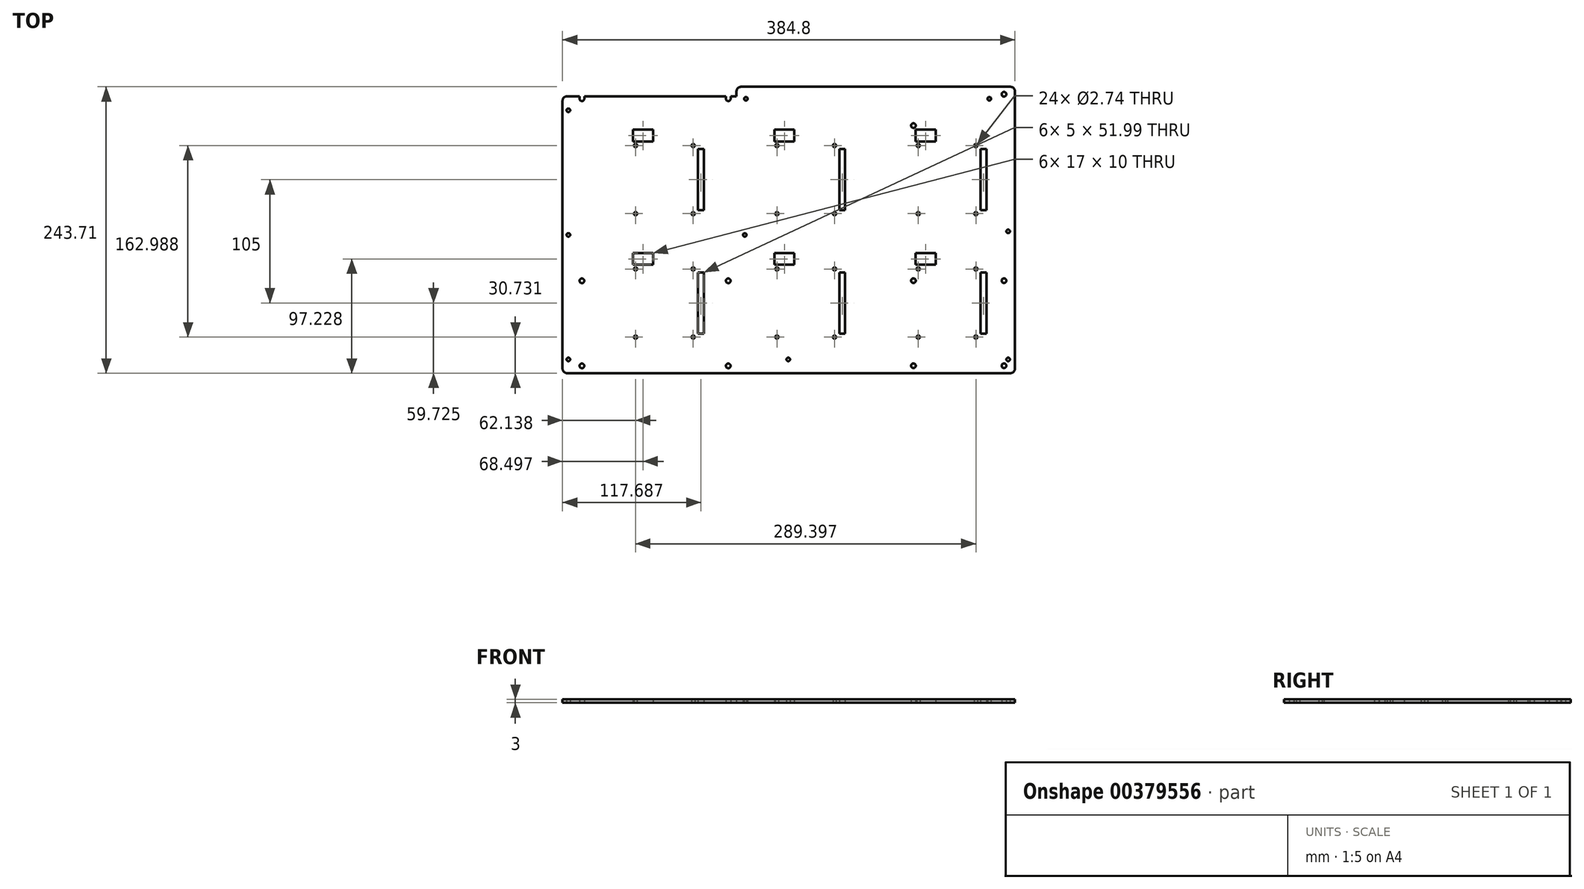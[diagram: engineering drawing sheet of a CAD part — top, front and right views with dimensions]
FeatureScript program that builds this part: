
annotation { "Feature Type Name" : "Feature", "Feature Type Description" : "" }
export const myFeature = defineFeature(function(context is Context, id is Id, definition is map)
    precondition{}
    {
        {
            var Q0;
            Q0=qCreatedBy(makeId("Top.planeOp"),FACE);
            var sketch = newSketch(context, id + "F0", { "sketchPlane" : qUnion([Q0])});
            skLineSegment(sketch, "E0.bottom", {"start": v(-157.61, -121.94) * mm, "end": v(139.26, -121.94) * mm});
            skLineSegment(sketch, "E0.left", {"start": v(-161.57, -117.98) * mm, "end": v(-161.57, 109.8) * mm});
            skArc(sketch, "E1", {"start": v(-147.04, 111.6) * mm, "mid": v(-145.06, 109.63) * mm, "end": v(-143.08, 111.6) * mm});
            skCircle(sketch, "E2", {"center": v(-145.06, -115.72) * mm, "radius": 1.98 * mm});
            skCircle(sketch, "E3", {"center": v(-145.06, -43.33) * mm, "radius": 1.98 * mm});
            skCircle(sketch, "E4", {"center": v(-20.6, -115.72) * mm, "radius": 1.98 * mm});
            skArc(sketch, "E5", {"start": v(-22.58, 111.6) * mm, "mid": v(-20.6, 109.63) * mm, "end": v(-18.62, 111.6) * mm});
            skCircle(sketch, "E6", {"center": v(136.88, 88.75) * mm, "radius": 1.98 * mm});
            skCircle(sketch, "E7", {"center": v(136.88, -115.6) * mm, "radius": 1.98 * mm});
            skCircle(sketch, "E8", {"center": v(136.88, -43.2) * mm, "radius": 1.98 * mm});
            skPoint(sketch, "E9.visualSharp", {"position": v(-161.57, -121.94) * mm});
            skArc(sketch, "E9.filletArc", {"start": v(-161.57, -117.98) * mm, "mid": v(-160.41, -120.78) * mm, "end": v(-157.61, -121.94) * mm});
            skCircle(sketch, "E10.MirrorC", {"center": v(-50.44, 13.8) * mm, "radius": 1.37 * mm});
            skCircle(sketch, "E11.MirrorC", {"center": v(-99.43, 71.78) * mm, "radius": 1.37 * mm});
            skCircle(sketch, "E12.MirrorC", {"center": v(-99.43, 13.8) * mm, "radius": 1.37 * mm});
            skCircle(sketch, "E13.MirrorC", {"center": v(-50.44, 71.78) * mm, "radius": 1.37 * mm});
            skLineSegment(sketch, "E14.bottom", {"start": v(-46.38, 68.78) * mm, "end": v(-41.38, 68.78) * mm});
            skLineSegment(sketch, "E14.top", {"start": v(-46.38, 16.8) * mm, "end": v(-41.38, 16.8) * mm});
            skLineSegment(sketch, "E14.left", {"start": v(-46.38, 68.78) * mm, "end": v(-46.38, 16.8) * mm});
            skLineSegment(sketch, "E14.right", {"start": v(-41.38, 68.78) * mm, "end": v(-41.38, 16.8) * mm});
            skCircle(sketch, "E15.MirrorC", {"center": v(-20.6, -43.33) * mm, "radius": 1.98 * mm});
            skCircle(sketch, "E16", {"center": v(-5.6, 111.6) * mm, "radius": 1.5 * mm});
            skCircle(sketch, "E17", {"center": v(-156.57, 101.77) * mm, "radius": 1.5 * mm});
            skLineSegment(sketch, "E18", {"start": v(-157.61, 113.77) * mm, "end": v(-147.04, 113.77) * mm});
            skLineSegment(sketch, "E19", {"start": v(-13.6, 117.8) * mm, "end": v(-13.6, 117.8) * mm});
            skLineSegment(sketch, "E20.trimOffspring", {"start": v(-9.64, 121.77) * mm, "end": v(143.23, 121.77) * mm});
            skPoint(sketch, "E21.visualSharp", {"position": v(-161.57, 113.77) * mm});
            skArc(sketch, "E21.filletArc", {"start": v(-157.61, 113.77) * mm, "mid": v(-160.41, 112.6) * mm, "end": v(-161.57, 109.8) * mm});
            skPoint(sketch, "E22.visualSharp", {"position": v(-13.6, 121.77) * mm});
            skArc(sketch, "E22.filletArc", {"start": v(-9.64, 121.77) * mm, "mid": v(-12.44, 120.6) * mm, "end": v(-13.6, 117.8) * mm});
            skPoint(sketch, "E23.visualSharp", {"position": v(-13.6, 113.77) * mm});
            skLineSegment(sketch, "E24", {"start": v(-147.04, 111.6) * mm, "end": v(-147.04, 113.77) * mm});
            skLineSegment(sketch, "E25", {"start": v(-143.08, 111.6) * mm, "end": v(-143.08, 113.77) * mm});
            skLineSegment(sketch, "E26.trimOffspring", {"start": v(-143.08, 113.77) * mm, "end": v(-22.58, 113.77) * mm, "construction": true});
            skLineSegment(sketch, "E27.trimOffspring", {"start": v(-143.08, 113.77) * mm, "end": v(-22.58, 113.77) * mm});
            skLineSegment(sketch, "E28", {"start": v(-22.58, 111.6) * mm, "end": v(-22.58, 113.77) * mm});
            skLineSegment(sketch, "E29", {"start": v(-18.62, 111.6) * mm, "end": v(-18.62, 113.77) * mm});
            skLineSegment(sketch, "E30.trimOffspring", {"start": v(-18.62, 113.77) * mm, "end": v(-13.6, 113.77) * mm});
            skLineSegment(sketch, "E31", {"start": v(-13.6, 113.77) * mm, "end": v(-13.6, 113.77) * mm});
            skLineSegment(sketch, "E32", {"start": v(-13.6, 113.77) * mm, "end": v(-13.6, 117.8) * mm});
            skLineSegment(sketch, "E33.bottom", {"start": v(-101.57, 85.29) * mm, "end": v(-84.57, 85.29) * mm});
            skLineSegment(sketch, "E33.top", {"start": v(-101.57, 75.29) * mm, "end": v(-84.57, 75.29) * mm});
            skLineSegment(sketch, "E33.left", {"start": v(-101.57, 85.29) * mm, "end": v(-101.57, 75.29) * mm});
            skLineSegment(sketch, "E34", {"start": v(-84.57, 85.29) * mm, "end": v(-84.57, 75.29) * mm});
            skLineSegment(sketch, "E35.1.0.0", {"start": v(18.63, 85.29) * mm, "end": v(35.63, 85.29) * mm});
            skLineSegment(sketch, "E35.1.0.1", {"start": v(18.63, 85.29) * mm, "end": v(18.63, 75.29) * mm});
            skLineSegment(sketch, "E35.1.0.2", {"start": v(78.82, 68.78) * mm, "end": v(78.82, 16.8) * mm});
            skLineSegment(sketch, "E35.1.0.3", {"start": v(73.82, 68.78) * mm, "end": v(73.82, 16.8) * mm});
            skLineSegment(sketch, "E35.1.0.4", {"start": v(18.63, 75.29) * mm, "end": v(35.63, 75.29) * mm});
            skCircle(sketch, "E35.1.0.5", {"center": v(20.77, 13.8) * mm, "radius": 1.37 * mm});
            skCircle(sketch, "E35.1.0.6", {"center": v(69.76, 13.8) * mm, "radius": 1.37 * mm});
            skLineSegment(sketch, "E35.1.0.7", {"start": v(35.63, 85.29) * mm, "end": v(35.63, 75.29) * mm});
            skCircle(sketch, "E35.1.0.8", {"center": v(69.76, 71.78) * mm, "radius": 1.37 * mm});
            skCircle(sketch, "E35.1.0.9", {"center": v(20.77, 71.78) * mm, "radius": 1.37 * mm});
            skLineSegment(sketch, "E35.1.0.10", {"start": v(73.82, 16.8) * mm, "end": v(78.82, 16.8) * mm});
            skLineSegment(sketch, "E35.1.0.11", {"start": v(73.82, 68.78) * mm, "end": v(78.82, 68.78) * mm});
            skLineSegment(sketch, "E35.2.0.0", {"start": v(138.83, 85.29) * mm, "end": v(155.83, 85.29) * mm});
            skLineSegment(sketch, "E35.2.0.1", {"start": v(138.83, 85.29) * mm, "end": v(138.83, 75.29) * mm});
            skLineSegment(sketch, "E35.2.0.2", {"start": v(199.02, 68.78) * mm, "end": v(199.02, 16.8) * mm});
            skLineSegment(sketch, "E35.2.0.3", {"start": v(194.02, 68.78) * mm, "end": v(194.02, 16.8) * mm});
            skLineSegment(sketch, "E35.2.0.4", {"start": v(138.83, 75.29) * mm, "end": v(155.83, 75.29) * mm});
            skCircle(sketch, "E35.2.0.5", {"center": v(140.97, 13.8) * mm, "radius": 1.37 * mm});
            skCircle(sketch, "E35.2.0.6", {"center": v(189.96, 13.8) * mm, "radius": 1.37 * mm});
            skLineSegment(sketch, "E35.2.0.7", {"start": v(155.83, 85.29) * mm, "end": v(155.83, 75.29) * mm});
            skCircle(sketch, "E35.2.0.8", {"center": v(189.96, 71.78) * mm, "radius": 1.37 * mm});
            skCircle(sketch, "E35.2.0.9", {"center": v(140.97, 71.78) * mm, "radius": 1.37 * mm});
            skLineSegment(sketch, "E35.2.0.10", {"start": v(194.02, 16.8) * mm, "end": v(199.02, 16.8) * mm});
            skLineSegment(sketch, "E35.2.0.11", {"start": v(194.02, 68.78) * mm, "end": v(199.02, 68.78) * mm});
            skLineSegment(sketch, "E36", {"start": v(143.23, 121.77) * mm, "end": v(219.27, 121.77) * mm});
            skLineSegment(sketch, "E37", {"start": v(223.23, 117.8) * mm, "end": v(223.23, -117.98) * mm});
            skLineSegment(sketch, "E38", {"start": v(219.27, -121.94) * mm, "end": v(139.26, -121.94) * mm});
            skPoint(sketch, "E39.visualSharp", {"position": v(223.23, 121.77) * mm});
            skArc(sketch, "E39.filletArc", {"start": v(223.23, 117.8) * mm, "mid": v(222.07, 120.6) * mm, "end": v(219.27, 121.77) * mm});
            skPoint(sketch, "E40.visualSharp", {"position": v(223.23, -121.94) * mm});
            skArc(sketch, "E40.filletArc", {"start": v(219.27, -121.94) * mm, "mid": v(222.07, -120.78) * mm, "end": v(223.23, -117.98) * mm});
            skCircle(sketch, "E41.1.0.0", {"center": v(213.88, -115.6) * mm, "radius": 1.98 * mm});
            skCircle(sketch, "E42.MirrorC", {"center": v(213.88, 115.42) * mm, "radius": 1.98 * mm});
            skCircle(sketch, "E43.1.0.0", {"center": v(213.88, -43.2) * mm, "radius": 1.98 * mm});
            skLineSegment(sketch, "E44.0.1.0", {"start": v(-41.38, -36.22) * mm, "end": v(-41.38, -88.2) * mm});
            skLineSegment(sketch, "E44.0.1.1", {"start": v(-101.57, -19.71) * mm, "end": v(-84.57, -19.71) * mm});
            skLineSegment(sketch, "E44.0.1.2", {"start": v(-101.57, -29.71) * mm, "end": v(-84.57, -29.71) * mm});
            skLineSegment(sketch, "E44.0.1.3", {"start": v(-46.38, -36.22) * mm, "end": v(-46.38, -88.2) * mm});
            skCircle(sketch, "E44.0.1.4", {"center": v(-50.44, -33.22) * mm, "radius": 1.37 * mm});
            skCircle(sketch, "E44.0.1.5", {"center": v(-50.44, -91.2) * mm, "radius": 1.37 * mm});
            skCircle(sketch, "E44.0.1.6", {"center": v(-99.43, -33.22) * mm, "radius": 1.37 * mm});
            skLineSegment(sketch, "E44.0.1.7", {"start": v(-84.57, -19.71) * mm, "end": v(-84.57, -29.71) * mm});
            skLineSegment(sketch, "E44.0.1.8", {"start": v(-46.38, -36.22) * mm, "end": v(-41.38, -36.22) * mm});
            skLineSegment(sketch, "E44.0.1.9", {"start": v(-46.38, -88.2) * mm, "end": v(-41.38, -88.2) * mm});
            skLineSegment(sketch, "E44.0.1.10", {"start": v(-101.57, -19.71) * mm, "end": v(-101.57, -29.71) * mm});
            skCircle(sketch, "E44.0.1.11", {"center": v(-99.43, -91.2) * mm, "radius": 1.37 * mm});
            skLineSegment(sketch, "E45.1.0.0", {"start": v(73.82, -36.22) * mm, "end": v(73.82, -88.2) * mm});
            skLineSegment(sketch, "E45.1.0.1", {"start": v(18.63, -19.71) * mm, "end": v(35.63, -19.71) * mm});
            skLineSegment(sketch, "E45.1.0.2", {"start": v(35.63, -19.71) * mm, "end": v(35.63, -29.71) * mm});
            skLineSegment(sketch, "E45.1.0.3", {"start": v(78.82, -36.22) * mm, "end": v(78.82, -88.2) * mm});
            skLineSegment(sketch, "E45.1.0.4", {"start": v(18.63, -19.71) * mm, "end": v(18.63, -29.71) * mm});
            skLineSegment(sketch, "E45.1.0.5", {"start": v(18.63, -29.71) * mm, "end": v(35.63, -29.71) * mm});
            skCircle(sketch, "E45.1.0.6", {"center": v(69.76, -33.22) * mm, "radius": 1.37 * mm});
            skCircle(sketch, "E45.1.0.7", {"center": v(20.77, -33.22) * mm, "radius": 1.37 * mm});
            skCircle(sketch, "E45.1.0.8", {"center": v(69.76, -91.2) * mm, "radius": 1.37 * mm});
            skCircle(sketch, "E45.1.0.9", {"center": v(20.77, -91.2) * mm, "radius": 1.37 * mm});
            skLineSegment(sketch, "E45.1.0.10", {"start": v(73.82, -36.22) * mm, "end": v(78.82, -36.22) * mm});
            skLineSegment(sketch, "E45.1.0.11", {"start": v(73.82, -88.2) * mm, "end": v(78.82, -88.2) * mm});
            skLineSegment(sketch, "E45.2.0.0", {"start": v(194.02, -36.22) * mm, "end": v(194.02, -88.2) * mm});
            skLineSegment(sketch, "E45.2.0.1", {"start": v(138.83, -19.71) * mm, "end": v(155.83, -19.71) * mm});
            skLineSegment(sketch, "E45.2.0.2", {"start": v(155.83, -19.71) * mm, "end": v(155.83, -29.71) * mm});
            skLineSegment(sketch, "E45.2.0.3", {"start": v(199.02, -36.22) * mm, "end": v(199.02, -88.2) * mm});
            skLineSegment(sketch, "E45.2.0.4", {"start": v(138.83, -19.71) * mm, "end": v(138.83, -29.71) * mm});
            skLineSegment(sketch, "E45.2.0.5", {"start": v(138.83, -29.71) * mm, "end": v(155.83, -29.71) * mm});
            skCircle(sketch, "E45.2.0.6", {"center": v(189.96, -33.22) * mm, "radius": 1.37 * mm});
            skCircle(sketch, "E45.2.0.7", {"center": v(140.97, -33.22) * mm, "radius": 1.37 * mm});
            skCircle(sketch, "E45.2.0.8", {"center": v(189.96, -91.2) * mm, "radius": 1.37 * mm});
            skCircle(sketch, "E45.2.0.9", {"center": v(140.97, -91.2) * mm, "radius": 1.37 * mm});
            skLineSegment(sketch, "E45.2.0.10", {"start": v(194.02, -36.22) * mm, "end": v(199.02, -36.22) * mm});
            skLineSegment(sketch, "E45.2.0.11", {"start": v(194.02, -88.2) * mm, "end": v(199.02, -88.2) * mm});
            skCircle(sketch, "E46.0.1.0", {"center": v(-156.57, -4.23) * mm, "radius": 1.5 * mm});
            skCircle(sketch, "E46.0.2.0", {"center": v(-156.57, -110.23) * mm, "radius": 1.5 * mm});
            skCircle(sketch, "E47.1.0.0", {"center": v(30.43, -110.23) * mm, "radius": 1.5 * mm});
            skCircle(sketch, "E47.2.0.0", {"center": v(217.43, -110.23) * mm, "radius": 1.5 * mm});
            skCircle(sketch, "E48.0.1.0", {"center": v(217.43, -1.23) * mm, "radius": 1.5 * mm});
            skCircle(sketch, "E49.1.0.0", {"center": v(201.4, 111.6) * mm, "radius": 1.5 * mm});
            skCircle(sketch, "E50.1.0.0", {"center": v(-6.57, -4.23) * mm, "radius": 1.5 * mm});
            skSolve(sketch);
        }
        {
            var Q0;
            Q0=makeQuery(id+"F0.imprint","IMPRINT",FACE,{"disambiguationData":[TD([[makeQuery(id+"F0.imprint","IMPRINT",EDGE,{"derivedFrom":sQuery(id+"F0.wireOp",EDGE,"E0.bottom")}),1.0]])]});
            extrude(context, id + "F1", {"entities" : qUnion([Q0]), "depth" : 3 * mm});
        }
    });
